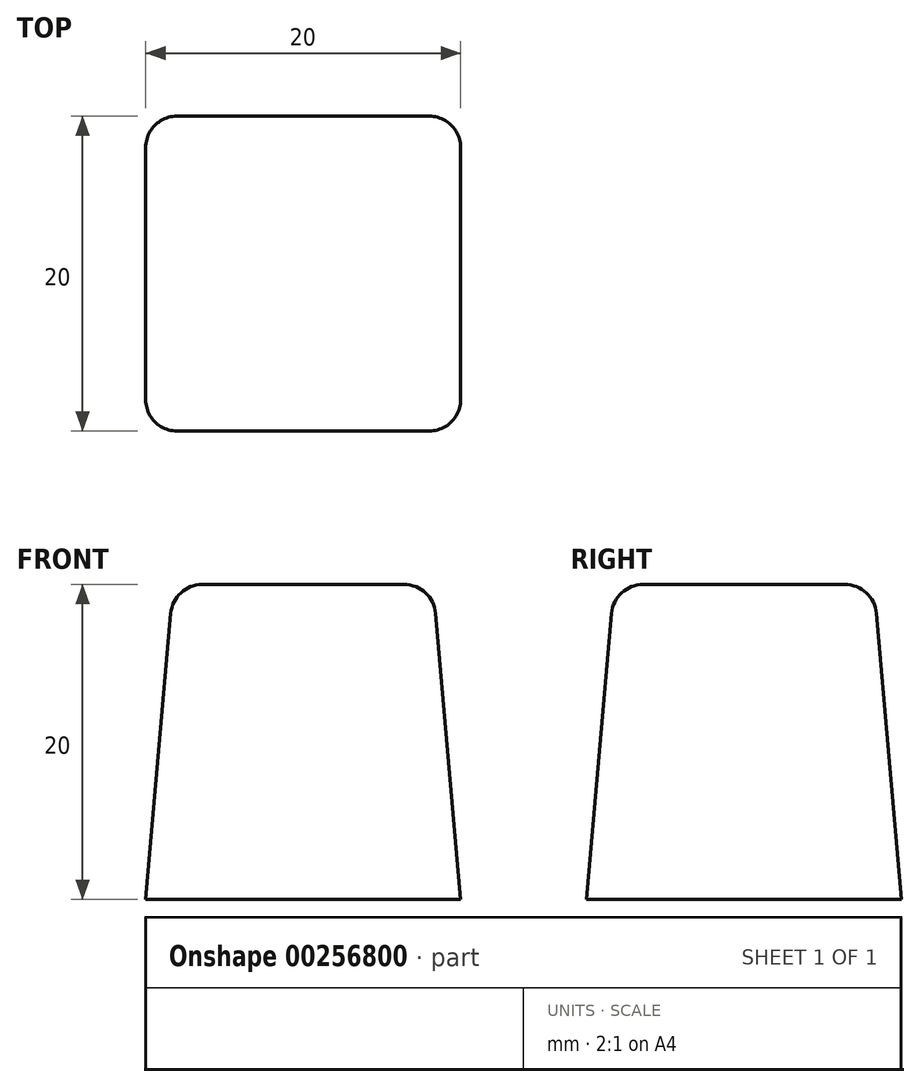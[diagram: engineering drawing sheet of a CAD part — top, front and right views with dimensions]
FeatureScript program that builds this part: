
annotation { "Feature Type Name" : "Feature", "Feature Type Description" : "" }
export const myFeature = defineFeature(function(context is Context, id is Id, definition is map)
    precondition{}
    {
        {
            var Q0;
            Q0=qCreatedBy(makeId("Top.planeOp"),FACE);
            var sketch = newSketch(context, id + "F0", { "sketchPlane" : qUnion([Q0])});
            skLineSegment(sketch, "E0.bottom", {"start": v(10, -10) * mm, "end": v(-10, -10) * mm});
            skLineSegment(sketch, "E0.top", {"start": v(10, 10) * mm, "end": v(-10, 10) * mm});
            skLineSegment(sketch, "E0.left", {"start": v(10, -10) * mm, "end": v(10, 10) * mm});
            skLineSegment(sketch, "E0.right", {"start": v(-10, -10) * mm, "end": v(-10, 10) * mm});
            skPoint(sketch, "E0.middle", {"position": v(0, 0) * mm});
            skSolve(sketch);
        }
        {
            var Q0;
            Q0=qSketchRegion(id+"F0",true);
            extrude(context, id + "F1", {"entities" : qUnion([Q0]), "depth" : 20 * mm, "hasDraft" : true, "draftAngle" : 5 * degree, "draftPullDirection" : true});
        }
        {
            var Q0;
            Q0=makeQuery(id+"F1.opExtrude","CAP_EDGE",EDGE,{"disambiguationData":[OSD([sQuery(id+"F0.wireOp",EDGE,"E0.top")])],"isStart":false});
            var Q1;
            Q1=makeQuery(id+"F1.opExtrude","CAP_EDGE",EDGE,{"disambiguationData":[OSD([sQuery(id+"F0.wireOp",EDGE,"E0.right")])],"isStart":false});
            var Q2;
            Q2=makeQuery(id+"F1.opExtrude","CAP_FACE",FACE,{"disambiguationData":[OSD([sQuery(id+"F0.wireOp",EDGE,"E0.bottom"),sQuery(id+"F0.wireOp",EDGE,"E0.top"),sQuery(id+"F0.wireOp",EDGE,"E0.left"),sQuery(id+"F0.wireOp",EDGE,"E0.right")])],"isStart":false});
            var Q3;
            Q3=makeQuery(id+"F1.opExtrude","SWEPT_EDGE",EDGE,{"disambiguationData":[OSD([sQuery(id+"F0.wireOp",EDGE,"E0.top"),sQuery(id+"F0.wireOp",EDGE,"E0.left")])]});
            var Q4;
            Q4=makeQuery(id+"F1.opExtrude","SWEPT_EDGE",EDGE,{"disambiguationData":[OSD([sQuery(id+"F0.wireOp",EDGE,"E0.top"),sQuery(id+"F0.wireOp",EDGE,"E0.right")])]});
            var Q5;
            Q5=makeQuery(id+"F1.opExtrude","SWEPT_EDGE",EDGE,{"disambiguationData":[OSD([sQuery(id+"F0.wireOp",EDGE,"E0.bottom"),sQuery(id+"F0.wireOp",EDGE,"E0.right")])]});
            var Q6;
            Q6=makeQuery(id+"F1.opExtrude","SWEPT_EDGE",EDGE,{"disambiguationData":[OSD([sQuery(id+"F0.wireOp",EDGE,"E0.bottom"),sQuery(id+"F0.wireOp",EDGE,"E0.left")])]});
            fillet(context, id + "F2", {"entities" : qUnion([Q0, Q1, Q2, Q3, Q4, Q5, Q6]), "radius" : 2 * mm, "tangentPropagation" : true, "allowEdgeOverflow" : false});
        }
    });
